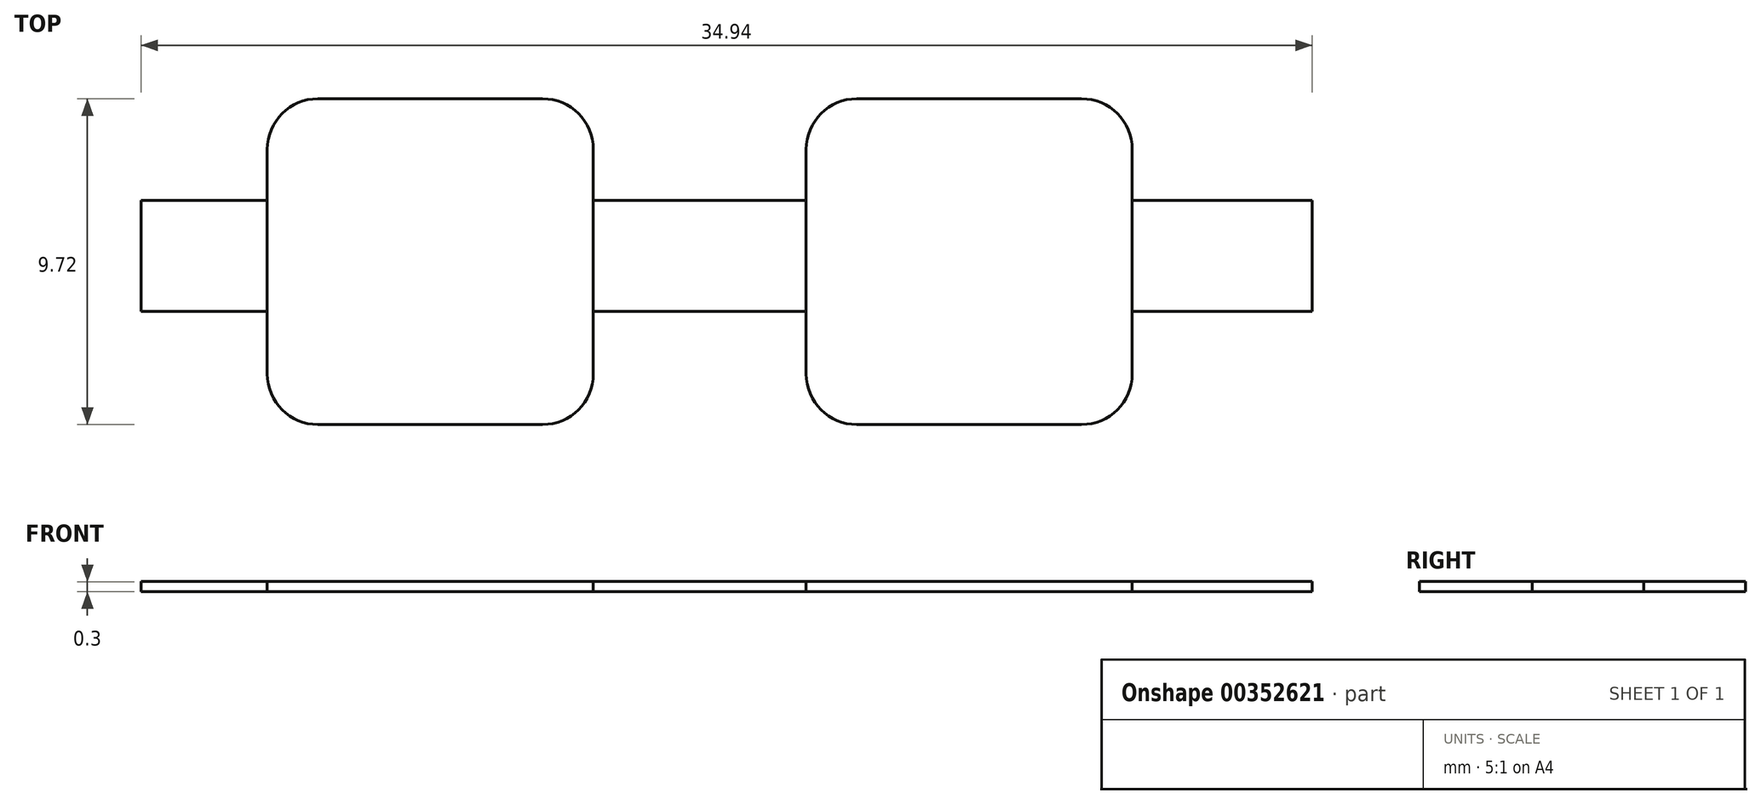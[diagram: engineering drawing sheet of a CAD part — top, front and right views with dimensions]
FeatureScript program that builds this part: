
annotation { "Feature Type Name" : "Feature", "Feature Type Description" : "" }
export const myFeature = defineFeature(function(context is Context, id is Id, definition is map)
    precondition{}
    {
        {
            var Q0;
            Q0=qCreatedBy(makeId("Top.planeOp"),FACE);
            var sketch = newSketch(context, id + "F0", { "sketchPlane" : qUnion([Q0])});
            skLineSegment(sketch, "E0.bottom", {"start": v(3.35, -4.86) * mm, "end": v(-3.35, -4.86) * mm});
            skLineSegment(sketch, "E0.top", {"start": v(3.35, 4.86) * mm, "end": v(-3.35, 4.86) * mm});
            skLineSegment(sketch, "E0.left", {"start": v(4.86, -3.35) * mm, "end": v(4.86, 3.35) * mm});
            skLineSegment(sketch, "E0.right", {"start": v(-4.86, -3.35) * mm, "end": v(-4.86, 3.35) * mm});
            skPoint(sketch, "E0.middle", {"position": v(0, 0) * mm});
            skLineSegment(sketch, "E1.bottom", {"start": v(-12.73, -4.86) * mm, "end": v(-19.43, -4.86) * mm});
            skLineSegment(sketch, "E1.top", {"start": v(-12.73, 4.86) * mm, "end": v(-19.43, 4.86) * mm});
            skLineSegment(sketch, "E1.left", {"start": v(-11.21, -3.35) * mm, "end": v(-11.21, 3.35) * mm});
            skLineSegment(sketch, "E1.right", {"start": v(-20.94, -3.35) * mm, "end": v(-20.94, 3.35) * mm});
            skPoint(sketch, "E1.middle", {"position": v(-16.08, 0) * mm});
            skPoint(sketch, "E2.visualSharp", {"position": v(-20.94, 4.86) * mm});
            skArc(sketch, "E2.filletArc", {"start": v(-19.43, 4.86) * mm, "mid": v(-20.5, 4.42) * mm, "end": v(-20.94, 3.35) * mm});
            skPoint(sketch, "E3.visualSharp", {"position": v(-11.21, 4.86) * mm});
            skArc(sketch, "E3.filletArc", {"start": v(-11.21, 3.35) * mm, "mid": v(-11.66, 4.42) * mm, "end": v(-12.73, 4.86) * mm});
            skPoint(sketch, "E4.visualSharp", {"position": v(-20.94, -4.86) * mm});
            skArc(sketch, "E4.filletArc", {"start": v(-20.94, -3.35) * mm, "mid": v(-20.5, -4.42) * mm, "end": v(-19.43, -4.86) * mm});
            skPoint(sketch, "E5.visualSharp", {"position": v(-11.21, -4.86) * mm});
            skArc(sketch, "E5.filletArc", {"start": v(-12.73, -4.86) * mm, "mid": v(-11.66, -4.42) * mm, "end": v(-11.21, -3.35) * mm});
            skPoint(sketch, "E6.visualSharp", {"position": v(-4.86, -4.86) * mm});
            skArc(sketch, "E6.filletArc", {"start": v(-4.86, -3.35) * mm, "mid": v(-4.42, -4.42) * mm, "end": v(-3.35, -4.86) * mm});
            skPoint(sketch, "E7.visualSharp", {"position": v(4.86, -4.86) * mm});
            skArc(sketch, "E7.filletArc", {"start": v(3.35, -4.86) * mm, "mid": v(4.42, -4.42) * mm, "end": v(4.86, -3.35) * mm});
            skPoint(sketch, "E8.visualSharp", {"position": v(4.86, 4.86) * mm});
            skArc(sketch, "E8.filletArc", {"start": v(4.86, 3.35) * mm, "mid": v(4.42, 4.42) * mm, "end": v(3.35, 4.86) * mm});
            skPoint(sketch, "E9.visualSharp", {"position": v(-4.86, 4.86) * mm});
            skArc(sketch, "E9.filletArc", {"start": v(-3.35, 4.86) * mm, "mid": v(-4.42, 4.42) * mm, "end": v(-4.86, 3.35) * mm});
            skLineSegment(sketch, "E10", {"start": v(-11.21, 1.83) * mm, "end": v(-4.86, 1.83) * mm});
            skLineSegment(sketch, "E11", {"start": v(-11.21, -1.49) * mm, "end": v(-4.86, -1.49) * mm});
            skLineSegment(sketch, "E12", {"start": v(4.86, 1.83) * mm, "end": v(10.23, 1.83) * mm});
            skLineSegment(sketch, "E13", {"start": v(4.86, -1.49) * mm, "end": v(10.23, -1.49) * mm});
            skLineSegment(sketch, "E14", {"start": v(10.23, -1.49) * mm, "end": v(10.23, 1.83) * mm});
            skLineSegment(sketch, "E15", {"start": v(-20.94, 1.83) * mm, "end": v(-24.71, 1.83) * mm});
            skLineSegment(sketch, "E16", {"start": v(-20.94, -1.49) * mm, "end": v(-24.71, -1.49) * mm});
            skLineSegment(sketch, "E17", {"start": v(-24.71, -1.49) * mm, "end": v(-24.71, 1.83) * mm});
            skSolve(sketch);
        }
        {
            var Q0;
            Q0=makeQuery(id+"F0.imprint","IMPRINT",FACE,{"disambiguationData":[TD([[makeQuery(id+"F0.imprint","IMPRINT",EDGE,{"derivedFrom":sQuery(id+"F0.wireOp",EDGE,"E1.bottom")}),-1.0]])]});
            var Q1;
            Q1=makeQuery(id+"F0.imprint","IMPRINT",FACE,{"disambiguationData":[TD([[makeQuery(id+"F0.imprint","IMPRINT",EDGE,{"derivedFrom":sQuery(id+"F0.wireOp",EDGE,"E0.bottom")}),-1.0]])]});
            extrude(context, id + "F1", {"entities" : qUnion([Q0, Q1]), "depth" : 0.3 * mm, "offsetDistance" : 25.4 * mm});
        }
        {
            var Q0;
            {var subQ0=sQuery(id+"F0.wireOp",EDGE,"E15");Q0=makeQuery(id+"F0.imprint","IMPRINT",FACE,{"disambiguationData":[TD([[makeQuery(id+"F0.imprint","IMPRINT",EDGE,{"derivedFrom":subQ0}),1.0]])]});}
            var Q1;
            {var subQ0=sQuery(id+"F0.wireOp",EDGE,"E10");Q1=makeQuery(id+"F0.imprint","IMPRINT",FACE,{"disambiguationData":[TD([[makeQuery(id+"F0.imprint","IMPRINT",EDGE,{"derivedFrom":subQ0}),-1.0]])]});}
            var Q2;
            {var subQ0=sQuery(id+"F0.wireOp",EDGE,"E12");Q2=makeQuery(id+"F0.imprint","IMPRINT",FACE,{"disambiguationData":[TD([[makeQuery(id+"F0.imprint","IMPRINT",EDGE,{"derivedFrom":subQ0}),-1.0]])]});}
            extrude(context, id + "F2", {"entities" : qUnion([Q0, Q1, Q2]), "depth" : 0.3 * mm, "offsetDistance" : 25.4 * mm});
        }
    });
